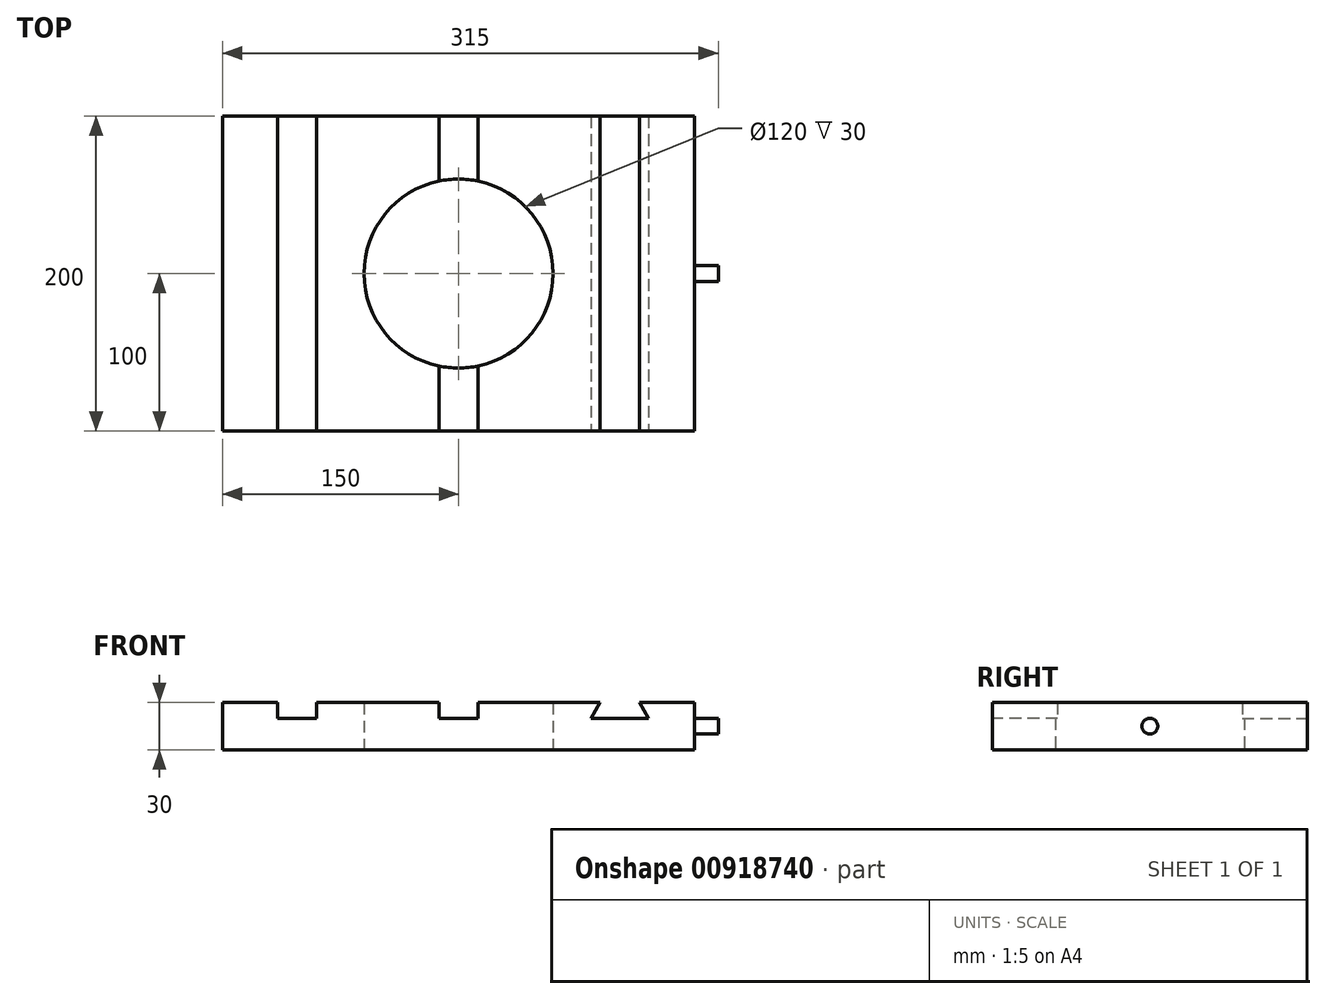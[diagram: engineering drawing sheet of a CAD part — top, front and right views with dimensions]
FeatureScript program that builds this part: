
annotation { "Feature Type Name" : "Feature", "Feature Type Description" : "" }
export const myFeature = defineFeature(function(context is Context, id is Id, definition is map)
    precondition{}
    {
        {
            var Q0;
            Q0=qCreatedBy(makeId("Top.planeOp"),FACE);
            var sketch = newSketch(context, id + "F0", { "sketchPlane" : qUnion([Q0])});
            skLineSegment(sketch, "E0.bottom", {"start": v(-150, 100) * mm, "end": v(150, 100) * mm});
            skLineSegment(sketch, "E0.top", {"start": v(-150, -100) * mm, "end": v(150, -100) * mm});
            skLineSegment(sketch, "E0.left", {"start": v(-150, 100) * mm, "end": v(-150, -100) * mm});
            skLineSegment(sketch, "E0.right", {"start": v(150, 100) * mm, "end": v(150, -100) * mm});
            skPoint(sketch, "E0.middle", {"position": v(0, 0) * mm});
            skCircle(sketch, "E1", {"center": v(0, 0) * mm, "radius": 60 * mm});
            skSolve(sketch);
        }
        {
            var Q0;
            Q0=makeQuery(id+"F0.imprint","IMPRINT",FACE,{"disambiguationData":[TD([[makeQuery(id+"F0.imprint","IMPRINT",EDGE,{"derivedFrom":sQuery(id+"F0.wireOp",EDGE,"E0.bottom")}),-1.0]])]});
            extrude(context, id + "F1", {"entities" : qUnion([Q0]), "depth" : 30 * mm, "offsetDistance" : 25 * mm});
        }
        {
            var Q0;
            Q0=makeQuery(id+"F1.opExtrude","CAP_FACE",FACE,{"disambiguationData":[OSD([sQuery(id+"F0.wireOp",EDGE,"E0.bottom"),sQuery(id+"F0.wireOp",EDGE,"E0.top"),sQuery(id+"F0.wireOp",EDGE,"E0.left"),sQuery(id+"F0.wireOp",EDGE,"E0.right"),sQuery(id+"F0.wireOp",EDGE,"E1")])],"isStart":false});
            var sketch = newSketch(context, id + "F2", { "sketchPlane" : qUnion([Q0])});
            skLineSegment(sketch, "E2.bottom", {"start": v(-115, 100) * mm, "end": v(-90, 100) * mm});
            skLineSegment(sketch, "E2.top", {"start": v(-115, -100) * mm, "end": v(-90, -100) * mm});
            skLineSegment(sketch, "E2.left", {"start": v(-115, 100) * mm, "end": v(-115, -100) * mm});
            skLineSegment(sketch, "E2.right", {"start": v(-90, 100) * mm, "end": v(-90, -100) * mm});
            skPoint(sketch, "E3", {"position": v(0, 0) * mm});
            skLineSegment(sketch, "E4", {"start": v(-12.5, 100) * mm, "end": v(-12.5, -100) * mm});
            skLineSegment(sketch, "E5", {"start": v(-12.5, -100) * mm, "end": v(12.5, -100) * mm});
            skLineSegment(sketch, "E6", {"start": v(12.5, -100) * mm, "end": v(12.5, 100) * mm});
            skLineSegment(sketch, "E7", {"start": v(12.5, 100) * mm, "end": v(-12.5, 100) * mm});
            skLineSegment(sketch, "E8", {"start": v(0, -100) * mm, "end": v(0, 100) * mm, "construction": true});
            skSolve(sketch);
        }
        {
            var Q0;
            Q0=makeQuery(id+"F2.imprint","IMPRINT",FACE,{"disambiguationData":[TD([[makeQuery(id+"F2.imprint","IMPRINT",EDGE,{"derivedFrom":sQuery(id+"F2.wireOp",EDGE,"E2.bottom")}),-1.0]])]});
            var Q1;
            Q1 = qSketchRegion(id + "F2", true);
            var Q2;
            {var subQ0=sQuery(id+"F2.wireOp",EDGE,"E5");Q2=makeQuery(id+"F2.imprint","IMPRINT",FACE,{"disambiguationData":[TD([[makeQuery(id+"F2.imprint","IMPRINT",EDGE,{"derivedFrom":subQ0}),1.0]])]});}
            var Q3;
            {var subQ0=sQuery(id+"F2.wireOp",EDGE,"E7");Q3=makeQuery(id+"F2.imprint","IMPRINT",FACE,{"disambiguationData":[TD([[makeQuery(id+"F2.imprint","IMPRINT",EDGE,{"derivedFrom":subQ0}),-1.0]])]});}
            extrude(context, id + "F3", {"entities" : qUnion([Q0, Q1, Q2, Q3]), "operationType" : NewBodyOperationType.REMOVE, "oppositeDirection" : true, "depth" : 10 * mm, "offsetDistance" : 25 * mm});
        }
        {
            var Q0;
            Q0=makeQuery(id+"F1.opExtrude","SWEPT_FACE",FACE,{"disambiguationData":[OSD([sQuery(id+"F0.wireOp",EDGE,"E0.top")])]});
            var sketch = newSketch(context, id + "F4", { "sketchPlane" : qUnion([Q0])});
            skLineSegment(sketch, "E9", {"start": v(90, 30) * mm, "end": v(84.23, 20) * mm});
            skLineSegment(sketch, "E10", {"start": v(84.23, 20) * mm, "end": v(120.77, 20) * mm});
            skLineSegment(sketch, "E11", {"start": v(120.77, 20) * mm, "end": v(115, 30) * mm});
            skLineSegment(sketch, "E12", {"start": v(115, 30) * mm, "end": v(90, 30) * mm});
            skLineSegment(sketch, "E13", {"start": v(102.5, 20) * mm, "end": v(102.5, 30) * mm, "construction": true});
            skSolve(sketch);
        }
        {
            var Q0;
            Q0=makeQuery(id+"F4.imprint","IMPRINT",FACE,{"disambiguationData":[TD([[makeQuery(id+"F4.imprint","IMPRINT",EDGE,{"derivedFrom":sQuery(id+"F4.wireOp",EDGE,"E9")}),1.0]])]});
            extrude(context, id + "F5", {"entities" : qUnion([Q0]), "operationType" : NewBodyOperationType.REMOVE, "endBound" : BoundingType.UP_TO_NEXT, "oppositeDirection" : true, "depth" : 25 * mm, "offsetDistance" : 25 * mm});
        }
        {
            var Q0;
            Q0=makeQuery(id+"F1.opExtrude","SWEPT_FACE",FACE,{"disambiguationData":[OSD([sQuery(id+"F0.wireOp",EDGE,"E0.right")])]});
            var sketch = newSketch(context, id + "F6", { "sketchPlane" : qUnion([Q0])});
            skCircle(sketch, "E14", {"center": v(0, 15) * mm, "radius": 5 * mm});
            skPoint(sketch, "E14.centerSnap0", {"position": v(-100, 15) * mm});
            skSolve(sketch);
        }
        {
            var Q0;
            Q0=makeQuery(id+"F6.imprint","IMPRINT",FACE,{"disambiguationData":[TD([[makeQuery(id+"F6.imprint","IMPRINT",EDGE,{"derivedFrom":sQuery(id+"F6.wireOp",EDGE,"E14")}),1.0]])]});
            extrude(context, id + "F7", {"entities" : qUnion([Q0]), "operationType" : NewBodyOperationType.ADD, "depth" : 15 * mm, "offsetDistance" : 25 * mm});
        }
    });
